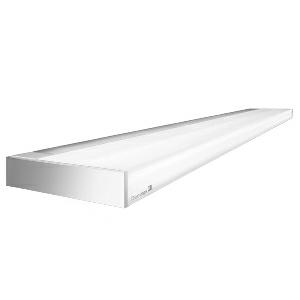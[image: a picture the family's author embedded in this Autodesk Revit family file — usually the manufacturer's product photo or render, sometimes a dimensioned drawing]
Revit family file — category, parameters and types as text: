
# Revit family: vanera_bed_-_vaw_8000_830_00812226_09e4
name_source: partatom
category: Lighting Fixtures
units: mm (PartAtom-declared; Revit-internal decimal feet)

## family parameters
Cut with Voids When Loaded = No
Host = Face
Light Source = No
Part Type = Normal
Room Calculation Point = No
Round Connector Dimension = Use Diameter
Shared = No

## types (1)
- AL+LL (1 x LED, 7500 lm, 3000K)
    Apparent Load = 71 VA
    Approval mark = CE
    CIE Flux Codes = 46 76 94 28 100
    Color Rendering = 80-89
    Color Temperature = 3000K
    Control Gear = Electronic ballast
    Default Elevation = 2000 mm  [stored 6.56168 ft]
    Description = VAW 8000/830|Wall-mounted luminaire|light source:   Warm white   |work equipment: Power supply unit|luminous flux: 7500 lm|light distribution: Direct/indirect|class of protection: I|technology: Two-stage switchable|mains lead: Connection box 3 pin|glare control: Diffusor|special features: General light, indirect, 3000K, Ra80, DIN EN 60598-2-25, Reading light, direct, 3,00K, Ra80|
    Frequency = 50 Hz, 60 Hz
    Height = 45 mm
    Lamp = 1 x LED
    Lamp Light Flux = 7500 lm
    Lamp count = 1
    Length = 1200 mm
    Luminous efficacy = 106 lm/W
    Manufacturer = Waldmann
    ModVariant = No
    Model = 00812226
    Mounting Place = Wall
    Mounting Type = Surface mounted
    Number of Poles = 1
    OnlyDefault = Yes
    Power Factor = 1
    Product Name = VANERA.bed - VAW 8000/830
    Product group = Wall mounted Luminaire
    ProductGroupID = 20
    Protection Class = Protection class I
    Protection Degree = Degree of protection
    RLX_Detail_Level = 1
    RLX_Emergency_Light_Flux = 0 lm
    RLX_Emergency_Type = 0
    RLX_Emergency_Type_DB = No
    RlxData = <blob elided: 62913 chars, md5=933eb637>
    Socket = socket
    Standby Power = 0 W
    System Light Flux = 7500 lm
    System Power = 71 W
    Type Comments = Allgemeinlicht und Leselicht
    Type Image = vanera_opal_54_54_w.jpg
    URL = http://relux.com
    VarID = al_ll_67c3
    Voltage = 230 V
    Voltage Range = 220-240 V
    Weight = 0.00 kg
    Width = 160 mm

note: [stored X ft] marks values corroborated as IEEE doubles in the binary element streams (Revit-internal decimal feet)

## geometry (parser evidence)
native form markers: Blend x4, Sweep x13
no freeform markers — native parametric forms only
